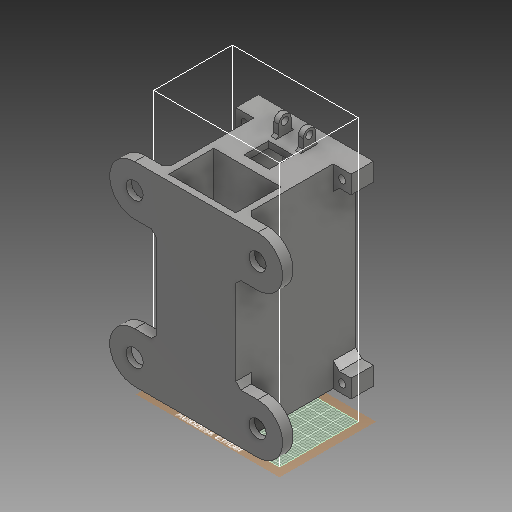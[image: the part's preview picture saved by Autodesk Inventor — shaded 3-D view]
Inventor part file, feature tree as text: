
AUTODESK INVENTOR PART (.ipt)
format: ipt  version: 2018 (Build 220112000, 112)  size: 1,320,448 bytes
history: native  units: in
note: dims shown in document units (in); Inventor stores cm internally (conversion verified against a paired STEP export)
features: sketch x33, extrude x30, move_body x15, direct_edit x10, chamfer x6, fillet x5, thicken_offset x3, delete_face x3, projected_geometry x1
ambient origin geometry x8: Origin, YZ Plane, XZ Plane, XY Plane, X Axis, Y Axis, Z Axis, Center Point
bodies: Solid1 (feature_tree)
feature tree (106):
  extrude  "Extrusion1"  Depth=0.125in
  extrude  "Extrusion2"  Depth=0.9in TaperAngle=0.0deg
  extrude  "Extrusion3"  Depth=2.0in
  extrude  "Extrusion4"  Depth=0.0625in
  sketch  "Sketch6"  dims[d11=0.5in d13=0.55in]
  extrude  "Extrusion6"  Depth=0.55in
  extrude  "Extrusion7"  Depth=0.725in
  extrude  "Extrusion8"  Depth=0.09in
  extrude  "Extrusion9"  Depth=0.125in
  extrude  "Extrusion10"  Depth=0.125in TaperAngle=0.0deg
  extrude  "Extrusion11"  Depth=0.7in
  extrude  "Extrusion12"  Depth=0.5in
  sketch  "Sketch16"  dims[d38=0.05in]
  extrude  "Extrusion13"  Depth=0.5in
  sketch  "Sketch18"  dims[d40=0.45in]
  fillet  "Fillet1"  Radius=0.05in
  chamfer  "Chamfer1"  Distance=0.36in
  chamfer  "Chamfer2"  Distance=0.25in
  extrude  "Extrusion14"  Depth=0.05in
  extrude  "Extrusion15"  Depth=0.35in
  extrude  "Extrusion16"  Depth=0.25in
  fillet  "Fillet2"  Radius=0.25in
  extrude  "Extrusion17"  Depth=0.1in
  chamfer  "Chamfer3"  Distance=0.125in Angle=45.0deg
  extrude  "Extrusion18"  Depth=0.125in
  extrude  "Extrusion19"  Depth=0.4in TaperAngle=0.0deg
  extrude  "Extrusion20"  Depth=0.05in
  extrude  "Extrusion21"  Depth=0.1in
  fillet  "Fillet3"  Radius=0.275in
  fillet  "Fillet4"  Radius=0.36in
  extrude  "Extrusion22"  Depth=0.225in
  extrude  "Extrusion23"  Depth=1.0in
  chamfer  "Chamfer4"  Distance=0.146in
  chamfer  "Chamfer5"  Distance=0.26in
  extrude  "Extrusion24"  Depth=0.123in
  extrude  "Extrusion25"  Depth=1.0in
  extrude  "Extrusion28"  Depth=1.0in
  extrude  "Extrusion29"  Depth=1.0in TaperAngle=0.0deg
  extrude  "Extrusion30"  Depth=0.125in TaperAngle=45.0deg
  extrude  "Extrusion31"  Depth=0.45in
  thicken_offset  "Thicken1"
  thicken_offset  "Thicken2"
  thicken_offset  "Thicken3"
  direct_edit  "Direct Edit1"
  direct_edit  "Direct Edit2"
  direct_edit  "Direct Edit3"
  direct_edit  "Direct Edit4"
  extrude  "Extrusion32"  Depth=1.0in TaperAngle=0.0deg
  fillet  "Fillet5"  Radius=0.125in
  chamfer  "Chamfer7"  Distance=0.125in
  direct_edit  "Direct Edit5"
  direct_edit  "Direct Edit6"
  direct_edit  "Direct Edit7"
  direct_edit  "Direct Edit8"
  delete_face  "Delete Face1"
  direct_edit  "Direct Edit9"
  delete_face  "Delete Face2"
  direct_edit  "Direct Edit10"
  delete_face  "Delete Face3"
  extrude  "Extrusion33"  Depth=1.0in
  sketch  "Sketch1"  dims[d0=0.125in d1=1.24in]
  sketch  "Sketch2"  dims[d2=0.9in d3=2.2in d4=0.0in]
  sketch  "Sketch3"  dims[d5=0.125in d6=0.0in d7=2.0in]
  sketch  "Sketch4"  dims[d8=0.125in d9=0.0in d10=0.0625in]
  sketch  "Sketch8"  dims[d14=0.125in d15=0.0in d16=0.725in]
  sketch  "Sketch10"  dims[d17=2.06in d21=0.09in]
  sketch  "Sketch11"  dims[d22=0.4in d23=0.0in d24=0.125in]
  sketch  "Sketch12"  dims[d25=1.475in d26=0.0in d27=0.125in d28=0.0in]
  sketch  "Sketch13"  dims[d29=0.6in d30=0.7in]
  sketch  "Sketch14"  dims[d31=0.5in d32=0.0in d33=0.1603in]
  sketch  "Sketch15"  dims[d34=0.5in d35=0.0in d36=0.146in d37=0.05in]
  sketch  "Sketch17"  dims[d39=0.1in]
  sketch  "Sketch19"  dims[d41=1.0in d42=0.36in d43=0.0in]
  sketch  "Sketch20"  dims[d44=0.225in]
  sketch  "Sketch21"  dims[d45=0.146in d46=0.25in d47=0.0in]
  sketch  "Sketch22"  dims[d49=0.05in d50=0.0in d51=0.05in]
  sketch  "Sketch24"  dims[d52=0.05in d53=0.35in]
  sketch  "Sketch25"  dims[d54=0.02in d55=0.02in d56=0.25in]
  sketch  "Sketch26"  dims[d57=0.25in d58=0.1in]
  sketch  "Sketch27"  dims[d59=0.0in]
  sketch  "Sketch28"  dims[d60=0.35in]
  sketch  "Sketch29"  dims[d61=0.346in]
  sketch  "Sketch30"  dims[d62=0.425in]
  sketch  "Sketch31"  dims[d63=0.9in]
  sketch  "Sketch34"  dims[d64=0.123in]
  sketch  "Sketch35"  dims[d65=0.123in d66=0.05in d67=0.125in d68=45.0deg]
  sketch  "Sketch36"  dims[d69=0.05in d70=0.125in d71=45.0deg d72=0.01in]
  sketch  "Sketch37"  dims[d73=0.4in d74=0.05in d75=0.0in]
  projected_geometry  "Projected Loop1"
  sketch  "Sketch38"  dims[d76=0.146in d77=0.05in]
  sketch  "Sketch39"  dims[d78=0.05in d80=0.1in d81=0.275in d82=0.36in d83=0.0in d84=0.225in d85=0.01in d86=0.146in d87=0.26in d88=0.0in d89=0.123in d90=0.05in d91=0.05in d92=0.05in d93=0.0in d94=0.05in d95=0.125in d96=45.0deg d97=0.45in d98=0.05in d99=0.0in d100=0.125in d101=0.0in d102=0.125in d103=0.0in d104=1.0in d105=1.0in d106=1.0in d107=0.912in d108=0.912in d109=0.912in d110=0.912in d111=0.21in d112=0.0in d113=0.5in d114=0.63in d115=0.63in d116=0.63in d117=0.63in d118=0.437in d119=0.437in d120=0.437in d121=0.437in d122=0.1in d123=0.0in d124=0.344in d125=0.344in d126=0.344in d127=0.344in d128=0.1in d129=0.0in d130=0.1in d131=0.125in d132=45.0deg d133=0.05in d134=0.125in d135=45.0deg d139=0.312in d140=0.3603in d141=0.3603in d142=0.3603in d143=0.3603in d144=0.3603in d145=0.45in d146=0.0in d147=0.146in d148=0.146in d149=0.146in d150=0.146in d151=0.5in d152=0.0in d163=1.0in d164=0.0in d165=0.35in d166=1.5in d168=0.3in d169=1.0in d170=0.0in d171=0.05in d172=0.3in d173=0.0in d174=0.05in d175=0.0in d176=0.1in d177=0.1in d178=0.1in d179=0.1in d180=0.1in d181=0.1in d182=0.0in d183=0.0in d184=0.1in d185=0.0in d186=0.0in d187=-0.1in d188=0.0in d189=0.0in d190=-0.05in d191=0.5in d192=0.0in d193=0.0in d194=0.05in d195=0.937in d196=0.937in d197=0.937in d198=0.937in d199=0.375in d200=0.0in d201=0.5in d202=0.125in d203=0.125in d204=45.0deg d205=0.0in d206=0.0in d207=-0.175in d208=0.0in d209=0.0in d210=0.35in d211=0.0in d212=0.0in d213=0.105in d214=0.0in d215=0.0in d216=0.105in d217=0.0in d218=0.0in d219=0.1in d220=0.0in d221=0.0in d222=0.1in d223=0.0in d224=0.0in d225=0.02in d226=0.0in d227=0.0in d228=0.09in d229=0.0in d230=0.0in d231=0.02in d232=0.0in d233=0.0in d234=0.09in d235=0.3in d236=0.0in d237=0.0in d238=0.16in d239=1.0in d240=0.0in]
  move_body  "Move1"
  move_body  "Move2"
  move_body  "Move3"
  move_body  "Move4"
  move_body  "Move5"
  move_body  "Move6"
  move_body  "Move7"
  move_body  "Move8"
  move_body  "Move9"
  move_body  "Move10"
  move_body  "Move11"
  move_body  "Move12"
  move_body  "Move13"
  move_body  "Move14"
  move_body  "Move15"
